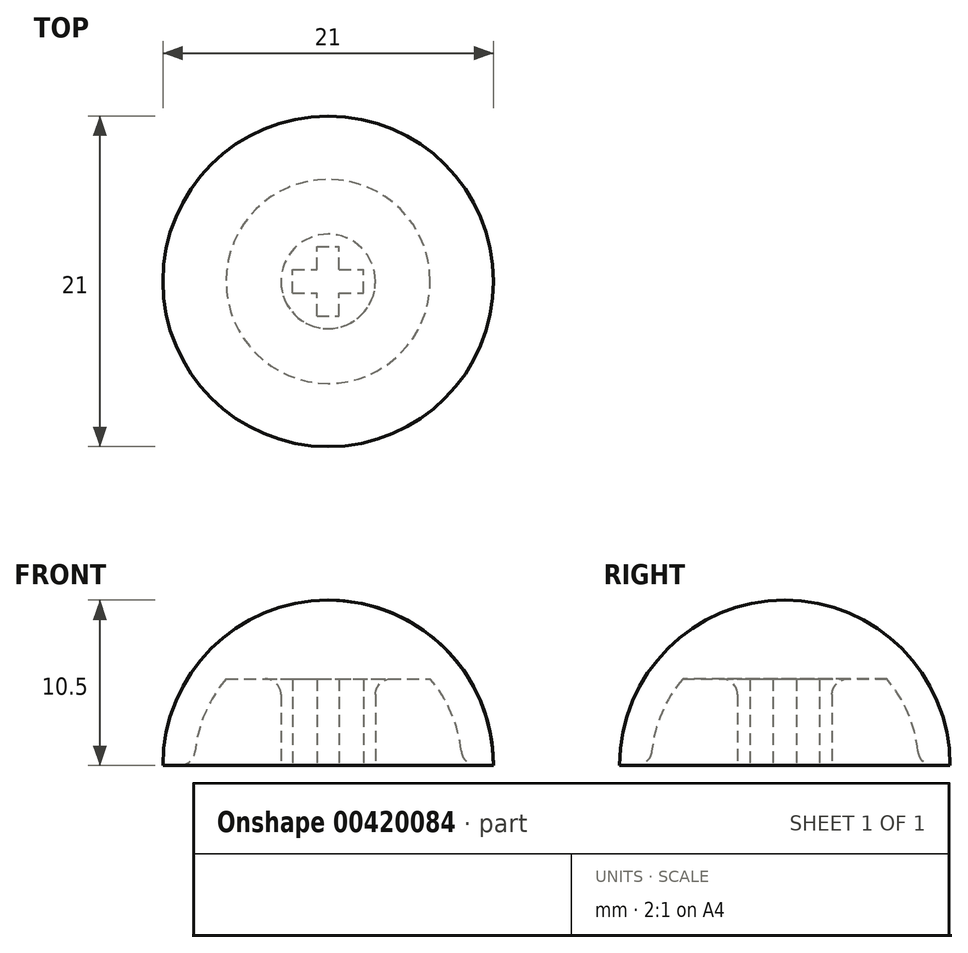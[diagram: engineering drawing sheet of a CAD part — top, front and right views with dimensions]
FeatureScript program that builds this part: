
annotation { "Feature Type Name" : "Feature", "Feature Type Description" : "" }
export const myFeature = defineFeature(function(context is Context, id is Id, definition is map)
    precondition{}
    {
        {
            var Q0;
            Q0=qCreatedBy(makeId("Front.planeOp"),FACE);
            var sketch = newSketch(context, id + "F0", { "sketchPlane" : qUnion([Q0])});
            skArc(sketch, "E0", {"start": v(10.5, 0) * mm, "mid": v(7.42, 7.42) * mm, "end": v(0, 10.5) * mm});
            skArc(sketch, "E1", {"start": v(8.5, 0) * mm, "mid": v(7.98, 2.93) * mm, "end": v(6.48, 5.5) * mm});
            skLineSegment(sketch, "E2", {"start": v(8.5, 0) * mm, "end": v(10.5, 0) * mm});
            skLineSegment(sketch, "E3", {"start": v(0, 9.5) * mm, "end": v(0, 10.5) * mm, "construction": true});
            skPoint(sketch, "E3.endSnap0", {"position": v(0, 10.5) * mm});
            skLineSegment(sketch, "E4", {"start": v(0, 10.5) * mm, "end": v(0, 8.5) * mm});
            skPoint(sketch, "E5.start.orphan", {"position": v(-10.5, 0) * mm});
            skPoint(sketch, "E6.orphan", {"position": v(0, 9.5) * mm});
            skLineSegment(sketch, "E7", {"start": v(0, 10.5) * mm, "end": v(0, 5.5) * mm});
            skLineSegment(sketch, "E8", {"start": v(0, 5.5) * mm, "end": v(6.48, 5.5) * mm});
            skSolve(sketch);
        }
        {
            var Q0;
            Q0=makeQuery(id+"F0.imprint","IMPRINT",FACE,{"disambiguationData":[TD([[makeQuery(id+"F0.imprint","IMPRINT",EDGE,{"derivedFrom":sQuery(id+"F0.wireOp",EDGE,"E0")}),1.0]])]});
            var Q1;
            Q1=sQuery(id+"F0.wireOp",EDGE,"E3");
            revolve(context, id + "F1", {"entities" : qUnion([Q0]), "axis" : qUnion([Q1]), "revolveType" : RevolveType.FULL});
        }
        {
            var Q0;
            Q0=qCreatedBy(makeId("Top.planeOp"),FACE);
            var sketch = newSketch(context, id + "F2", { "sketchPlane" : qUnion([Q0])});
            skCircle(sketch, "E9", {"center": v(0, 0) * mm, "radius": 3 * mm});
            skLineSegment(sketch, "E10.bottom", {"start": v(-0.7, -2.2) * mm, "end": v(0.7, -2.2) * mm});
            skLineSegment(sketch, "E10.top", {"start": v(-0.7, 2.2) * mm, "end": v(0.7, 2.2) * mm});
            skLineSegment(sketch, "E10.left", {"start": v(-0.7, -2.2) * mm, "end": v(-0.7, -0.75) * mm});
            skLineSegment(sketch, "E10.right", {"start": v(0.7, -2.2) * mm, "end": v(0.7, -0.75) * mm});
            skLineSegment(sketch, "E11.bottom", {"start": v(-2.25, -0.75) * mm, "end": v(-0.7, -0.75) * mm});
            skLineSegment(sketch, "E11.top", {"start": v(-2.25, 0.75) * mm, "end": v(-0.7, 0.75) * mm});
            skLineSegment(sketch, "E11.left", {"start": v(-2.25, -0.75) * mm, "end": v(-2.25, 0.75) * mm});
            skLineSegment(sketch, "E11.right", {"start": v(2.25, -0.75) * mm, "end": v(2.25, 0.75) * mm});
            skLineSegment(sketch, "E12", {"start": v(0, 0) * mm, "end": v(0.7, 0) * mm, "construction": true});
            skPoint(sketch, "E13.orphan", {"position": v(0, -2.2) * mm});
            skLineSegment(sketch, "E14", {"start": v(0, 0) * mm, "end": v(0, -2.2) * mm, "construction": true});
            skLineSegment(sketch, "E15", {"start": v(0, 0) * mm, "end": v(0, 0.75) * mm, "construction": true});
            skLineSegment(sketch, "E16.trimOffspring", {"start": v(0.7, 0.75) * mm, "end": v(0.7, 2.2) * mm});
            skLineSegment(sketch, "E17", {"start": v(0.7, -0.75) * mm, "end": v(0.7, 0.75) * mm, "construction": true});
            skLineSegment(sketch, "E18.trimOffspring", {"start": v(0.7, -0.75) * mm, "end": v(2.25, -0.75) * mm});
            skLineSegment(sketch, "E19.trimOffspring", {"start": v(-0.7, 0.75) * mm, "end": v(-0.7, 2.2) * mm});
            skLineSegment(sketch, "E20.trimOffspring", {"start": v(0.7, 0.75) * mm, "end": v(2.25, 0.75) * mm});
            skLineSegment(sketch, "E21", {"start": v(0.7, 0.75) * mm, "end": v(-0.7, 0.75) * mm, "construction": true});
            skPoint(sketch, "E22.end.orphan", {"position": v(-2.25, 0) * mm});
            skLineSegment(sketch, "E23", {"start": v(0, 0) * mm, "end": v(-2.25, 0) * mm, "construction": true});
            skSolve(sketch);
        }
        {
            var Q0;
            Q0=makeQuery(id+"F2.imprint","IMPRINT",FACE,{"disambiguationData":[TD([[makeQuery(id+"F2.imprint","IMPRINT",EDGE,{"derivedFrom":sQuery(id+"F2.wireOp",EDGE,"E9")}),1.0]])]});
            extrude(context, id + "F3", {"entities" : qUnion([Q0]), "operationType" : NewBodyOperationType.ADD, "depth" : 6 * mm});
        }
        {
            var Q0;
            Q0=makeQuery(id+"F3.boolean.opBoolean","INTERSECT",EDGE,{"derivedFrom":[makeQuery(id+"F1.opRevolve","SWEPT_FACE",FACE,{"disambiguationData":[OSD([sQuery(id+"F0.wireOp",EDGE,"E8")])]}),makeQuery(id+"F3.opExtrude","SWEPT_FACE",FACE,{"disambiguationData":[OSD([sQuery(id+"F2.wireOp",EDGE,"E9")])]})]});
            fillet(context, id + "F4", {"entities" : qUnion([Q0]), "radius" : 1 * mm, "tangentPropagation" : true, "allowEdgeOverflow" : false});
        }
        {
            var Q0;
            Q0=makeQuery(id+"F1.opRevolve","SWEPT_EDGE",EDGE,{"disambiguationData":[OSD([sQuery(id+"F0.wireOp",EDGE,"E1"),sQuery(id+"F0.wireOp",EDGE,"E2")])]});
            fillet(context, id + "F5", {"entities" : qUnion([Q0]), "radius" : 1 * mm, "tangentPropagation" : true, "allowEdgeOverflow" : false});
        }
    });
